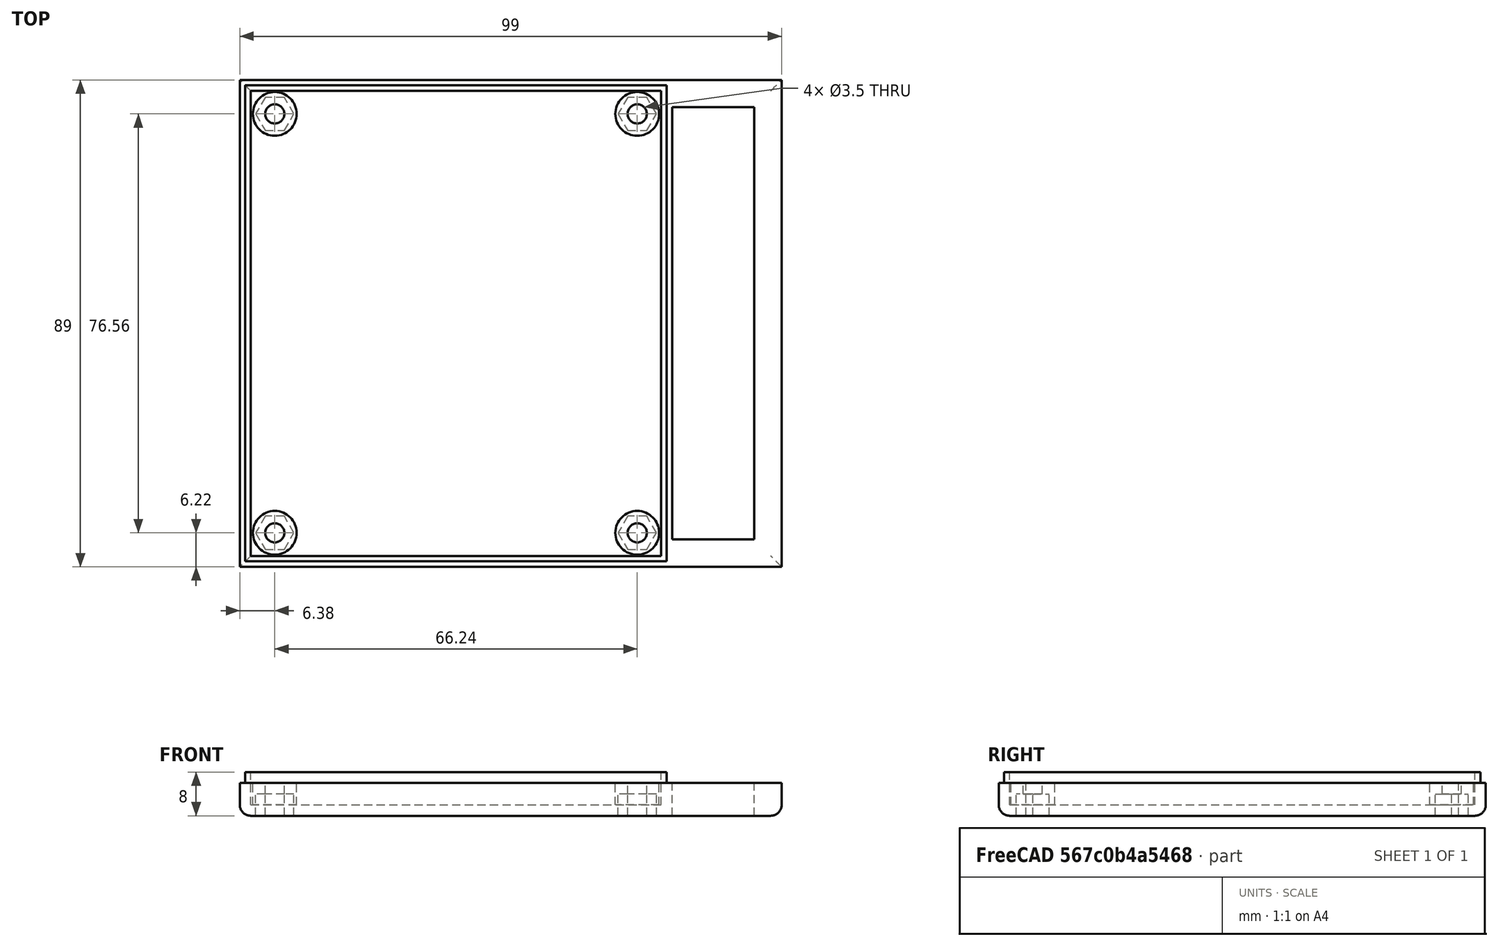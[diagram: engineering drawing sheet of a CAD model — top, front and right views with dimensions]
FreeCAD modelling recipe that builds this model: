
FCSTD DOCUMENT  (FreeCAD 0.18R16131 (Git))
Label: remote_case
License: All rights reserved
LicenseURL: http://en.wikipedia.org/wiki/All_rights_reserved
objects: Part::Cut×15, Part::Cylinder×12, Part::Box×7, Part::MultiFuse×6, Part::Prism×4, Part::Fillet×2
note: 46 computed .brp shape members not serialized (recipe doc carries the construction recipe); baked Part::Feature solids carry a one-line shape summary decoded from their .brp

FEATURE [Part::Box] Box  label="Cube"
  AttacherType = Attacher::AttachEngine3D
  Height = 10
  Length = 75
  Placement = pos=(0,0,2) rot=(0,0,1;0rad)
  Width = 85
FEATURE [Part::Cylinder] Cylinder
  Angle = 360
  AttacherType = Attacher::AttachEngine3D
  Height = 10
  Placement = pos=(4.38,80.78,0) rot=(0,0,1;0rad)
  Radius = 1.75
FEATURE [Part::Cylinder] Cylinder001
  Angle = 360
  AttacherType = Attacher::AttachEngine3D
  Height = 10
  Placement = pos=(70.62,80.78,0) rot=(0,0,1;0rad)
  Radius = 1.75
FEATURE [Part::Cylinder] Cylinder002
  Angle = 360
  AttacherType = Attacher::AttachEngine3D
  Height = 10
  Placement = pos=(70.62,4.22,0) rot=(0,0,1;0rad)
  Radius = 1.75
FEATURE [Part::Cylinder] Cylinder003
  Angle = 360
  AttacherType = Attacher::AttachEngine3D
  Height = 10
  Placement = pos=(4.38,4.22,0) rot=(0,0,1;0rad)
  Radius = 1.75
FEATURE [Part::Box] Box001  label="Cube001"
  AttacherType = Attacher::AttachEngine3D
  Height = 8
  Length = 79
  Placement = pos=(-2,-2,0) rot=(0,0,1;0rad)
  Width = 89
FEATURE [Part::Cut] Cut
  Base = -> Box001
  Tool = -> Box
FEATURE [Part::Cut] Cut001
  Base = -> Cut
  Tool = -> Cylinder003
FEATURE [Part::Cut] Cut002
  Base = -> Cut001
  Tool = -> Cylinder002
FEATURE [Part::Cut] Cut003
  Base = -> Cut002
  Tool = -> Cylinder001
FEATURE [Part::Cut] Cut004
  Base = -> Cut003
  Tool = -> Cylinder
FEATURE [Part::Cylinder] Cylinder004
  Angle = 360
  AttacherType = Attacher::AttachEngine3D
  Height = 4
  Placement = pos=(4.38,4.22,2) rot=(0,0,1;0rad)
  Radius = 4
FEATURE [Part::Prism] Prism
  AttacherType = Attacher::AttachEngine3D
  Circumradius = 3.5
  Height = 4
  Placement = pos=(4.38,4.22,0) rot=(0,0,1;0rad)
  Polygon = 6
FEATURE [Part::Cylinder] Cylinder005
  Angle = 360
  AttacherType = Attacher::AttachEngine3D
  Height = 10
  Placement = pos=(4.38,4.22,-1) rot=(0,0,1;0rad)
  Radius = 1.75
FEATURE [Part::Prism] Prism001
  AttacherType = Attacher::AttachEngine3D
  Circumradius = 3.5
  Height = 4
  Placement = pos=(70.62,4.22,0) rot=(0,0,1;0rad)
  Polygon = 6
FEATURE [Part::Prism] Prism002
  AttacherType = Attacher::AttachEngine3D
  Circumradius = 3.5
  Height = 4
  Placement = pos=(70.62,80.78,0) rot=(0,0,1;0rad)
  Polygon = 6
FEATURE [Part::Prism] Prism003
  AttacherType = Attacher::AttachEngine3D
  Circumradius = 3.5
  Height = 4
  Placement = pos=(4.38,80.78,0) rot=(0,0,1;0rad)
  Polygon = 6
FEATURE [Part::Cylinder] Cylinder006
  Angle = 360
  AttacherType = Attacher::AttachEngine3D
  Height = 10
  Placement = pos=(70.62,4.22,-1) rot=(0,0,1;0rad)
  Radius = 1.75
FEATURE [Part::Cylinder] Cylinder007
  Angle = 360
  AttacherType = Attacher::AttachEngine3D
  Height = 10
  Placement = pos=(70.62,80.78,-1) rot=(0,0,1;0rad)
  Radius = 1.75
FEATURE [Part::Cylinder] Cylinder008
  Angle = 360
  AttacherType = Attacher::AttachEngine3D
  Height = 10
  Placement = pos=(4.38,80.78,-1) rot=(0,0,1;0rad)
  Radius = 1.75
FEATURE [Part::Cylinder] Cylinder009
  Angle = 360
  AttacherType = Attacher::AttachEngine3D
  Height = 4
  Placement = pos=(70.62,4.22,2) rot=(0,0,1;0rad)
  Radius = 4
FEATURE [Part::Cylinder] Cylinder010
  Angle = 360
  AttacherType = Attacher::AttachEngine3D
  Height = 4
  Placement = pos=(70.62,80.78,2) rot=(0,0,1;0rad)
  Radius = 4
FEATURE [Part::Cylinder] Cylinder011
  Angle = 360
  AttacherType = Attacher::AttachEngine3D
  Height = 4
  Placement = pos=(4.38,80.78,2) rot=(0,0,1;0rad)
  Radius = 4
FEATURE [Part::MultiFuse] Fusion
  Shapes = -> [Cylinder011,Cut004]
FEATURE [Part::MultiFuse] Fusion001
  Shapes = -> [Cylinder010,Fusion]
FEATURE [Part::MultiFuse] Fusion002
  Shapes = -> [Cylinder009,Fusion001]
FEATURE [Part::MultiFuse] Fusion003
  Shapes = -> [Cylinder004,Fusion002]
FEATURE [Part::Cut] Cut005
  Base = -> Fusion003
  Tool = -> Prism003
FEATURE [Part::Cut] Cut006
  Base = -> Cut005
  Tool = -> Prism002
FEATURE [Part::Cut] Cut007
  Base = -> Cut006
  Tool = -> Prism001
FEATURE [Part::Cut] Cut008
  Base = -> Cut007
  Tool = -> Prism
FEATURE [Part::Cut] Cut009
  Base = -> Cut008
  Tool = -> Cylinder008
FEATURE [Part::Cut] Cut010
  Base = -> Cut009
  Tool = -> Cylinder007
FEATURE [Part::Cut] Cut011
  Base = -> Cut010
  Tool = -> Cylinder006
FEATURE [Part::Cut] Cut012
  Base = -> Cut011
  Tool = -> Cylinder005
FEATURE [Part::Box] Box002  label="Cube002"
  AttacherType = Attacher::AttachEngine3D
  Height = 10
  Length = 79
  Placement = pos=(-2,-2,10) rot=(0,0,1;0rad)
  Width = 89
FEATURE [Part::Box] Box003  label="Cube003"
  AttacherType = Attacher::AttachEngine3D
  Height = 10
  Length = 77
  Placement = pos=(-1,-1,10) rot=(0,0,1;0rad)
  Width = 87
FEATURE [Part::Cut] Cut013
  Base = -> Box002
  Placement = pos=(0,0,-4) rot=(0,0,1;0rad)
  Tool = -> Box003
FEATURE [Part::Cut] Cut014
  Base = -> Cut012
  Tool = -> Cut013
FEATURE [Part::Box] Box004  label="Cube004"
  AttacherType = Attacher::AttachEngine3D
  Height = 6
  Length = 15
  Placement = pos=(77,-2,0) rot=(0,0,1;0rad)
  Width = 5
FEATURE [Part::Box] Box005  label="Cube005"
  AttacherType = Attacher::AttachEngine3D
  Height = 6
  Length = 15
  Placement = pos=(77,82,0) rot=(0,0,1;0rad)
  Width = 5
FEATURE [Part::Box] Box006  label="Cube006"
  AttacherType = Attacher::AttachEngine3D
  Height = 6
  Length = 5
  Placement = pos=(92,-2,0) rot=(0,0,1;0rad)
  Width = 89
FEATURE [Part::MultiFuse] Fusion004
  Shapes = -> [Box004,Box005,Box006]
FEATURE [Part::Fillet] Fillet
  Base = -> Fusion004
  Edges = 3 edges r=2: [Edge5,Edge24,Edge33]
FEATURE [Part::Fillet] Fillet001
  Base = -> Cut014
  Edges = 3 edges r=2: [Edge67,Edge68,Edge69]
FEATURE [Part::MultiFuse] Fusion005
  Shapes = -> [Fillet,Fillet001]
